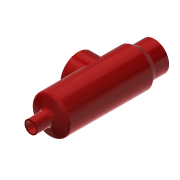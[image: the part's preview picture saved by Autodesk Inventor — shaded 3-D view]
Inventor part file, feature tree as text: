
AUTODESK INVENTOR PART (.ipt)
format: ipt  version: 2019.4 (Build 234330000, 330)  size: 171,520 bytes
history: native  units: mm
features: sketch x4, extrude x3, other x3, fillet x2, reference x2, revolve x1, projected_geometry x1
ambient origin geometry x8: Origin, YZ Plane, XZ Plane, XY Plane, X Axis, Y Axis, Z Axis, Center Point
bodies: Solid1 (feature_tree)
feature tree (16):
  revolve  "Revolution1"  [1 undecoded]
  extrude  "Extrusion3"  Depth=9.115mm
  extrude  "Extrusion4"  Depth=10.0mm
  sketch  "Sketch7"  dims[d21=6.4mm d22=10.0mm d23=0.0mm d24=2.0mm d25=65.0mm d26=0.3mm d27=15.0mm d28=0.0mm d29=15.0mm d30=-0.698132mm d31=2.0mm]
  fillet  "Fillet2"  Radius=10.0mm
  extrude  "Extrusion2"  Depth=10.0mm TaperAngle=0.0deg
  fillet  "Fillet3"  Radius=2.0mm
  sketch  "Sketch1"  dims[d6=90.0deg d12=4.0mm]
  reference  "Reference1"
  sketch  "Sketch4"  dims[d13=0.0mm d15=9.115mm]
  reference  "Reference2"
  projected_geometry  "Projected Loop2"
  sketch  "Sketch5"  dims[d17=2.0mm d19=5.0mm d20=10.0mm]
  other  "Assemlby_OpenOxygen.iam"
  other  "00_Sensirion_Flowsensor:1"
  other  "01_Connector_T:1"
note: 1 required parameter value undecoded (feature->parameter linkage not recoverable at this tier; creation-order binding heuristic only, values carry confidence <= 0.55)
